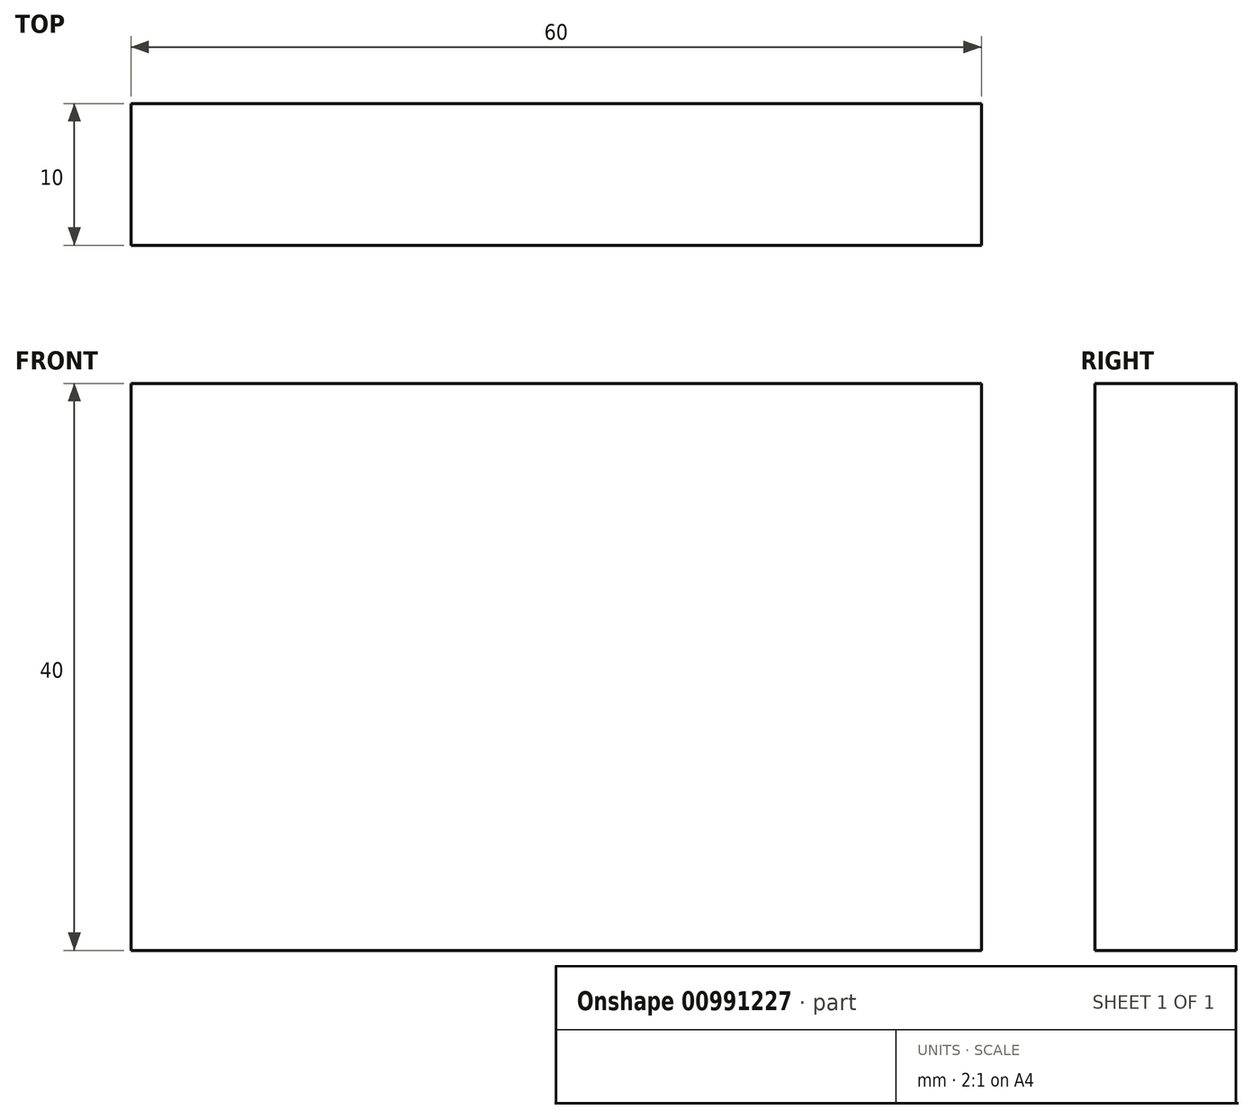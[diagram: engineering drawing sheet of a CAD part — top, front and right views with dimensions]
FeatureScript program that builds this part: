
annotation { "Feature Type Name" : "Feature", "Feature Type Description" : "" }
export const myFeature = defineFeature(function(context is Context, id is Id, definition is map)
    precondition{}
    {
        {
            var Q0;
            Q0=qCreatedBy(makeId("Front.planeOp"),FACE);
            var sketch = newSketch(context, id + "F0", { "sketchPlane" : qUnion([Q0])});
            skLineSegment(sketch, "E0.bottom", {"start": v(0, 0) * mm, "end": v(60, 0) * mm});
            skLineSegment(sketch, "E0.top", {"start": v(0, 40) * mm, "end": v(60, 40) * mm});
            skLineSegment(sketch, "E0.left", {"start": v(0, 0) * mm, "end": v(0, 40) * mm});
            skLineSegment(sketch, "E0.right", {"start": v(60, 0) * mm, "end": v(60, 40) * mm});
            skSolve(sketch);
        }
        {
            var Q0;
            Q0 = qSketchRegion(id + "F0", true);
            extrude(context, id + "F1", {"entities" : qUnion([Q0]), "depth" : 10 * mm, "offsetDistance" : 25 * mm});
        }
    });
